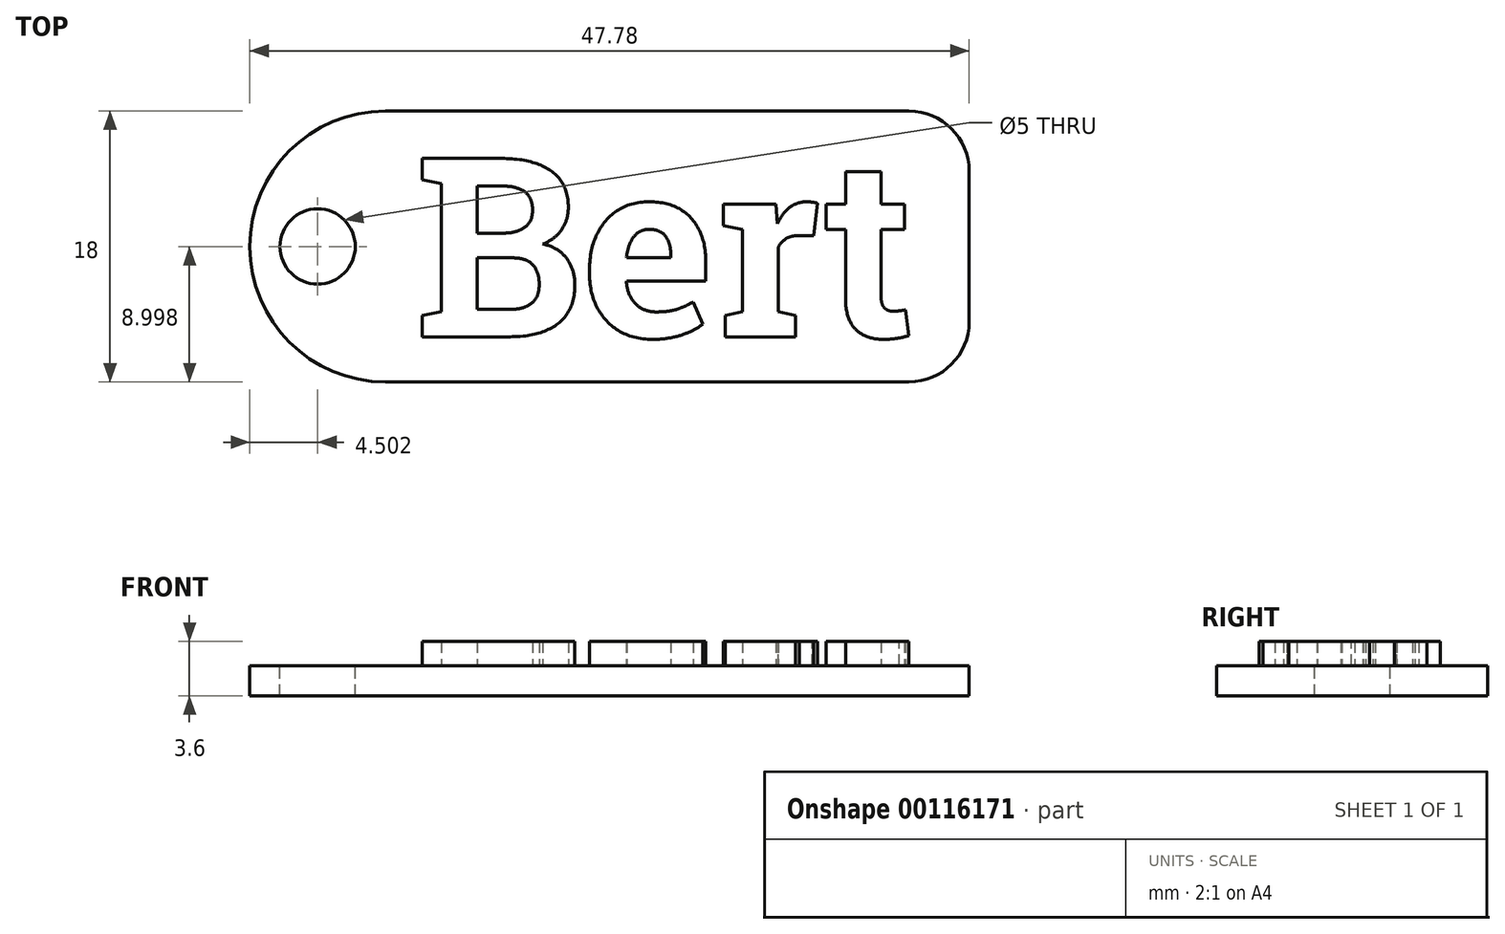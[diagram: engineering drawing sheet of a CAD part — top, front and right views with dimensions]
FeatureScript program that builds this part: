
annotation { "Feature Type Name" : "Feature", "Feature Type Description" : "" }
export const myFeature = defineFeature(function(context is Context, id is Id, definition is map)
    precondition{}
    {
        {
            var Q0;
            Q0=qCreatedBy(makeId("Top.planeOp"),FACE);
            var sketch = newSketch(context, id + "F0", { "sketchPlane" : qUnion([Q0])});
            skText(sketch, "E0", { "text": "Bert", "fontName": "RobotoSlab-Bold.ttf"});
            skLineSegment(sketch, "E1", {"start": v(-21.69, 9.04) * mm, "end": v(-21.69, -8.96) * mm});
            skLineSegment(sketch, "E2", {"start": v(-21.69, -8.96) * mm, "end": v(17.09, -8.96) * mm});
            skLineSegment(sketch, "E3", {"start": v(17.09, -8.96) * mm, "end": v(17.09, 9.04) * mm});
            skLineSegment(sketch, "E4", {"start": v(17.09, 9.04) * mm, "end": v(-21.69, 9.04) * mm});
            skArc(sketch, "E5", {"start": v(-21.69, 9.04) * mm, "mid": v(-30.69, 0.04) * mm, "end": v(-21.69, -8.96) * mm});
            skCircle(sketch, "E6", {"center": v(-26.19, 0.04) * mm, "radius": 2.5 * mm});
            skLineSegment(sketch, "E7", {"start": v(-21.69, 0.04) * mm, "end": v(-30.69, 0.04) * mm, "construction": true});
            const initialGuessF0  = {"E0": [-0.01969, -0.00596, 1, 0, 0.012]};
            skSetInitialGuess(sketch, initialGuessF0);
            skSolve(sketch);
        }
        {
            var Q0;
            Q0=makeQuery(id+"F0.imprint","IMPRINT",FACE,{"disambiguationData":[TD([[makeQuery(id+"F0.imprint","IMPRINT",EDGE,{"derivedFrom":sQuery(id+"F0.wireOp",EDGE,"E1")}),-1.0]])]});
            var Q1;
            Q1=makeQuery(id+"F0.imprint","IMPRINT",FACE,{"disambiguationData":[TD([[makeQuery(id+"F0.imprint","IMPRINT",EDGE,{"derivedFrom":sQuery(id+"F0.wireOp",EDGE,"E0.sketch_text.stroke-0")}),1.0]])]});
            var Q2;
            Q2 = qSketchRegion(id + "F0", true);
            var Q3;
            Q3=makeQuery(id+"F0.imprint","IMPRINT",FACE,{"disambiguationData":[TD([[makeQuery(id+"F0.imprint","IMPRINT",EDGE,{"derivedFrom":sQuery(id+"F0.wireOp",EDGE,"E0.sketch_text.stroke-89")}),-1.0]])]});
            var Q4;
            Q4=makeQuery(id+"F0.imprint","IMPRINT",FACE,{"disambiguationData":[TD([[makeQuery(id+"F0.imprint","IMPRINT",EDGE,{"derivedFrom":sQuery(id+"F0.wireOp",EDGE,"E0.sketch_text.stroke-24")}),-1.0]])]});
            var Q5;
            Q5=makeQuery(id+"F0.imprint","IMPRINT",FACE,{"disambiguationData":[TD([[makeQuery(id+"F0.imprint","IMPRINT",EDGE,{"derivedFrom":sQuery(id+"F0.wireOp",EDGE,"E0.sketch_text.stroke-113")}),-1.0]])]});
            var Q6;
            Q6=makeQuery(id+"F0.imprint","IMPRINT",FACE,{"disambiguationData":[TD([[makeQuery(id+"F0.imprint","IMPRINT",EDGE,{"derivedFrom":sQuery(id+"F0.wireOp",EDGE,"E0.sketch_text.stroke-106")}),1.0]])]});
            var Q7;
            Q7=makeQuery(id+"F0.imprint","IMPRINT",FACE,{"disambiguationData":[TD([[makeQuery(id+"F0.imprint","IMPRINT",EDGE,{"derivedFrom":sQuery(id+"F0.wireOp",EDGE,"E0.sketch_text.stroke-69")}),-1.0]])]});
            var Q8;
            Q8=makeQuery(id+"F0.imprint","IMPRINT",FACE,{"disambiguationData":[TD([[makeQuery(id+"F0.imprint","IMPRINT",EDGE,{"derivedFrom":sQuery(id+"F0.wireOp",EDGE,"E0.sketch_text.stroke-59")}),-1.0]])]});
            var Q9;
            Q9=makeQuery(id+"F0.imprint","IMPRINT",FACE,{"disambiguationData":[TD([[makeQuery(id+"F0.imprint","IMPRINT",EDGE,{"derivedFrom":sQuery(id+"F0.wireOp",EDGE,"E0.sketch_text.stroke-51")}),1.0]])]});
            var Q10;
            Q10=makeQuery(id+"F0.imprint","IMPRINT",FACE,{"disambiguationData":[TD([[makeQuery(id+"F0.imprint","IMPRINT",EDGE,{"derivedFrom":sQuery(id+"F0.wireOp",EDGE,"E0.sketch_text.stroke-0")}),-1.0]])]});
            var Q11;
            Q11=makeQuery(id+"F0.imprint","IMPRINT",FACE,{"disambiguationData":[TD([[makeQuery(id+"F0.imprint","IMPRINT",EDGE,{"derivedFrom":sQuery(id+"F0.wireOp",EDGE,"E0.sketch_text.stroke-23")}),1.0]])]});
            var Q12;
            Q12=makeQuery(id+"F0.imprint","IMPRINT",FACE,{"disambiguationData":[TD([[makeQuery(id+"F0.imprint","IMPRINT",EDGE,{"derivedFrom":sQuery(id+"F0.wireOp",EDGE,"E0.sketch_text.stroke-16")}),1.0]])]});
            var Q13;
            Q13=makeQuery(id+"F0.imprint","IMPRINT",FACE,{"disambiguationData":[TD([[makeQuery(id+"F0.imprint","IMPRINT",EDGE,{"derivedFrom":sQuery(id+"F0.wireOp",EDGE,"E0.sketch_text.stroke-30")}),-1.0]])]});
            var Q14;
            Q14=makeQuery(id+"F0.imprint","IMPRINT",FACE,{"disambiguationData":[TD([[makeQuery(id+"F0.imprint","IMPRINT",EDGE,{"derivedFrom":sQuery(id+"F0.wireOp",EDGE,"E0.sketch_text.stroke-76")}),1.0]])]});
            var Q15;
            Q15=makeQuery(id+"F0.imprint","IMPRINT",FACE,{"disambiguationData":[TD([[makeQuery(id+"F0.imprint","IMPRINT",EDGE,{"derivedFrom":sQuery(id+"F0.wireOp",EDGE,"E0.sketch_text.stroke-129")}),1.0]])]});
            var Q16;
            Q16=makeQuery(id+"F0.imprint","IMPRINT",FACE,{"disambiguationData":[TD([[makeQuery(id+"F0.imprint","IMPRINT",EDGE,{"derivedFrom":sQuery(id+"F0.wireOp",EDGE,"E0.sketch_text.stroke-139")}),-1.0]])]});
            var Q17;
            Q17=makeQuery(id+"F0.imprint","IMPRINT",FACE,{"disambiguationData":[TD([[makeQuery(id+"F0.imprint","IMPRINT",EDGE,{"derivedFrom":sQuery(id+"F0.wireOp",EDGE,"E0.sketch_text.stroke-149")}),-1.0]])]});
            var Q18;
            Q18=makeQuery(id+"F0.imprint","IMPRINT",FACE,{"disambiguationData":[TD([[makeQuery(id+"F0.imprint","IMPRINT",EDGE,{"derivedFrom":sQuery(id+"F0.wireOp",EDGE,"E0.sketch_text.stroke-24")}),1.0]])]});
            var Q19;
            Q19=makeQuery(id+"F0.imprint","IMPRINT",FACE,{"disambiguationData":[TD([[makeQuery(id+"F0.imprint","IMPRINT",EDGE,{"derivedFrom":sQuery(id+"F0.wireOp",EDGE,"E0.sketch_text.stroke-34")}),-1.0]])]});
            var Q20;
            Q20=makeQuery(id+"F0.imprint","IMPRINT",FACE,{"disambiguationData":[TD([[makeQuery(id+"F0.imprint","IMPRINT",EDGE,{"derivedFrom":sQuery(id+"F0.wireOp",EDGE,"E0.sketch_text.stroke-28")}),1.0]])]});
            var Q21;
            Q21=makeQuery(id+"F0.imprint","IMPRINT",FACE,{"disambiguationData":[TD([[makeQuery(id+"F0.imprint","IMPRINT",EDGE,{"derivedFrom":sQuery(id+"F0.wireOp",EDGE,"E0.sketch_text.stroke-55")}),1.0]])]});
            extrude(context, id + "F1", {"entities" : qUnion([Q0, Q1, Q2, Q3, Q4, Q5, Q6, Q7, Q8, Q9, Q10, Q11, Q12, Q13, Q14, Q15, Q16, Q17, Q18, Q19, Q20, Q21]), "oppositeDirection" : true, "depth" : 2 * mm});
        }
        {
            var Q0;
            Q0=makeQuery(id+"F0.imprint","IMPRINT",FACE,{"disambiguationData":[TD([[makeQuery(id+"F0.imprint","IMPRINT",EDGE,{"derivedFrom":sQuery(id+"F0.wireOp",EDGE,"E0.sketch_text.stroke-0")}),-1.0]])]});
            var Q1;
            Q1=makeQuery(id+"F0.imprint","IMPRINT",FACE,{"disambiguationData":[TD([[makeQuery(id+"F0.imprint","IMPRINT",EDGE,{"derivedFrom":sQuery(id+"F0.wireOp",EDGE,"E0.sketch_text.stroke-14")}),-1.0]])]});
            var Q2;
            Q2=makeQuery(id+"F0.imprint","IMPRINT",FACE,{"disambiguationData":[TD([[makeQuery(id+"F0.imprint","IMPRINT",EDGE,{"derivedFrom":sQuery(id+"F0.wireOp",EDGE,"E0.sketch_text.stroke-34")}),-1.0]])]});
            var Q3;
            Q3=makeQuery(id+"F0.imprint","IMPRINT",FACE,{"disambiguationData":[TD([[makeQuery(id+"F0.imprint","IMPRINT",EDGE,{"derivedFrom":sQuery(id+"F0.wireOp",EDGE,"E0.sketch_text.stroke-58")}),-1.0]])]});
            var Q4;
            Q4=makeQuery(id+"F0.imprint","IMPRINT",FACE,{"disambiguationData":[TD([[makeQuery(id+"F0.imprint","IMPRINT",EDGE,{"derivedFrom":sQuery(id+"F0.wireOp",EDGE,"E0.sketch_text.stroke-73")}),-1.0]])]});
            extrude(context, id + "F2", {"entities" : qUnion([Q0, Q1, Q2, Q3, Q4]), "operationType" : NewBodyOperationType.ADD, "depth" : 1.6 * mm});
        }
        {
            var Q0;
            Q0=makeQuery(id+"F1.opExtrude","SWEPT_EDGE",EDGE,{"disambiguationData":[OSD([sQuery(id+"F0.wireOp",EDGE,"E2"),sQuery(id+"F0.wireOp",EDGE,"E3")])]});
            var Q1;
            Q1=makeQuery(id+"F1.opExtrude","SWEPT_EDGE",EDGE,{"disambiguationData":[OSD([sQuery(id+"F0.wireOp",EDGE,"E3"),sQuery(id+"F0.wireOp",EDGE,"E4")])]});
            fillet(context, id + "F3", {"entities" : qUnion([Q0, Q1]), "radius" : 4 * mm, "tangentPropagation" : true, "allowEdgeOverflow" : false});
        }
    });
